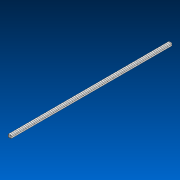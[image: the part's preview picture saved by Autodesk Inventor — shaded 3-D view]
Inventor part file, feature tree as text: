
AUTODESK INVENTOR PART (.ipt)
format: ipt  version: 2022.2 (Build 262287000, 287)  size: 887,296 bytes
history: native  units: in
note: dims shown in document units (in); Inventor stores cm internally (conversion verified against a paired STEP export)
features: other x59, extrude x1, pattern_linear x1, sketch x1, pattern_circular x1
ambient origin geometry x8: Origin, YZ Plane, XZ Plane, XY Plane, X Axis, Y Axis, Z Axis, Center Point
bodies: Solid1 (feature_tree)
feature tree (63):
  extrude  "Extrusion1"  TaperAngle=0.0deg  [1 undecoded]
  other  "Work Axis1"
  pattern_linear  "Rectangular Pattern1"  Spacing1=0.0in  [1 undecoded]
  sketch  "Sketch1"  dims[d0=1.0in d1=0.0in d2=0.0in d3=23.2283in d5=1.0in]
  other  "Work Axis2"
  other  "Work Axis3"
  other  "Work Axis4"
  other  "Work Axis5"
  other  "Work Axis6"
  other  "Work Axis7"
  other  "Work Axis8"
  other  "Work Axis9"
  other  "Work Axis10"
  other  "Work Axis11"
  other  "Work Axis12"
  other  "Work Axis13"
  other  "Work Axis14"
  other  "Work Axis15"
  other  "Work Axis16"
  other  "Work Axis17"
  other  "Work Axis18"
  other  "Work Axis19"
  other  "Work Axis20"
  other  "Work Axis21"
  other  "Work Axis22"
  other  "Work Axis23"
  other  "Work Axis24"
  other  "Work Axis25"
  other  "Work Axis26"
  other  "Work Axis27"
  other  "Work Axis28"
  other  "Work Axis29"
  other  "Work Axis30"
  other  "Work Axis31"
  other  "Work Axis32"
  other  "Work Axis33"
  other  "Work Axis34"
  other  "Work Axis35"
  other  "Work Axis36"
  other  "Work Axis37"
  other  "Work Axis38"
  other  "Work Axis39"
  other  "Work Axis40"
  other  "Work Axis41"
  other  "Work Axis42"
  other  "Work Axis43"
  other  "Work Axis44"
  other  "Work Axis45"
  other  "Work Axis46"
  other  "Work Axis47"
  other  "Work Axis48"
  other  "Work Axis49"
  other  "Work Axis50"
  other  "Work Axis51"
  other  "Work Axis52"
  other  "Work Axis53"
  other  "Work Axis54"
  other  "Work Axis55"
  other  "Work Axis56"
  other  "Work Axis57"
  other  "Work Axis58"
  other  "Work Axis59"
  pattern_circular  "CirPattern2"
note: 2 required parameter values undecoded (feature->parameter linkage not recoverable at this tier; creation-order binding heuristic only, values carry confidence <= 0.55)
